# Revit family: TR3105
name_source: partatom
category: Verbindungsmittel
units: mm (PartAtom-declared; Revit-internal decimal feet)

## family parameters
Arbeitsebenenbasiert = Nein
Beim Laden mit Abzugskörper schneiden = Nein
Gemeinsam genutzt = Nein
Immer vertikal = Nein
OmniClass-Nummer = 23.25.10.27.11.21
OmniClass-Titel = Reinforcement Couplers

## types (10) — shared parameters
Endenbearbeitung 1 = Mit Gewinde
Endenbearbeitung 2 = Mit Gewinde
Hersteller = Stahlwerk Annahütte Max Aicher GmbH Co.KG
Modell = TR 3105=TR3014+TR3013
TR3105-G_Vis = Ja
TR3105_Vis = Ja
Typenbild = TR3105.png
Typenkommentare = TR 3105 - Spannschloss
URL = http//:www.annahuette.com

## per-type parameters (varying)
| type | Außendurchmesser | Beschreibung | Einfassung Stab 1 | Einfassung Stab 2 | Gesamtlänge | Körper | Pos_TR3014 | Stabgröße 1 | Stabgröße 2 | TR3013-L0 | TR3013-Lm | TR3013-Lw | TR3013-SW | TR3013-ød | TR3014-L | TR3014-L1 | TR3014-L2 | TR3014-SW | TR3105-G | TR3105-minA | TR3105-ød |
| TR 3105-ø18 | 41 mm  [stored 0.134514 ft] | TR3105-ø18 | 50 mm  [stored 0.164042 ft] | 60 mm  [stored 0.19685 ft] | 175 mm | 1,34 kg | 73 mm | SAS 670 - ø18 | SAS 670 - ø18 | 15 mm  [stored 0.0492126 ft] | 45 mm  [stored 0.147638 ft] | 60 mm  [stored 0.19685 ft] | 41 mm  [stored 0.134514 ft] | 21 mm  [stored 0.0688976 ft] | 145 mm  [stored 0.475722 ft] | 50 mm  [stored 0.164042 ft] | 45 mm  [stored 0.147638 ft] | 41 mm  [stored 0.134514 ft] | 1,34 kg | 30 mm  [stored 0.0984252 ft] | 18 mm  [stored 0.0590551 ft] |
| TR 3105-ø22 | 46 mm  [stored 0.150919 ft] | TR3105-ø22 | 55 mm  [stored 0.180446 ft] | 65 mm  [stored 0.213255 ft] | 190 mm | 1,78 kg | 80 mm  [stored 0.262467 ft] | SAS 670 - ø22 | SAS 670 - ø22 | 15 mm  [stored 0.0492126 ft] | 50 mm  [stored 0.164042 ft] | 65 mm  [stored 0.213255 ft] | 46 mm  [stored 0.150919 ft] | 25 mm  [stored 0.082021 ft] | 160 mm | 55 mm  [stored 0.180446 ft] | 50 mm  [stored 0.164042 ft] | 46 mm  [stored 0.150919 ft] | 1,78 kg | 35 mm  [stored 0.114829 ft] | 22 mm  [stored 0.0721785 ft] |
| TR 3105-ø25 | 55 mm  [stored 0.180446 ft] | TR3105-ø25 | 60 mm  [stored 0.19685 ft] | 70 mm  [stored 0.229659 ft] | 205 mm | 2,94 kg | 88 mm | SAS 670 - ø25 | SAS 670 - ø25 | 15 mm  [stored 0.0492126 ft] | 55 mm  [stored 0.180446 ft] | 70 mm  [stored 0.229659 ft] | 55 mm  [stored 0.180446 ft] | 28 mm  [stored 0.0918635 ft] | 175 mm | 60 mm  [stored 0.19685 ft] | 55 mm  [stored 0.180446 ft] | 55 mm  [stored 0.180446 ft] | 2,94 kg | 40 mm  [stored 0.131234 ft] | 25 mm  [stored 0.082021 ft] |
| TR 3105-ø28 | 50 mm  [stored 0.164042 ft] | TR3105-ø28 | 65 mm  [stored 0.213255 ft] | 80 mm  [stored 0.262467 ft] | 225 mm | 3,74 kg | 95 mm | SAS 670 - ø28 | SAS 670 - ø28 | 20 mm  [stored 0.0656168 ft] | 60 mm  [stored 0.19685 ft] | 80 mm  [stored 0.262467 ft] | 60 mm  [stored 0.19685 ft] | 31 mm  [stored 0.101706 ft] | 190 mm | 65 mm  [stored 0.213255 ft] | 60 mm  [stored 0.19685 ft] | 50 mm  [stored 0.164042 ft] | 3,74 kg | 45 mm  [stored 0.147638 ft] | 28 mm  [stored 0.0918635 ft] |
| TR 3105-ø30 | 65 mm  [stored 0.213255 ft] | TR3105-ø30 | 70 mm  [stored 0.229659 ft] | 95 mm | 260 mm | 5,11 kg | 108 mm | SAS 670 - ø30 | SAS 670 - ø30 | 25 mm  [stored 0.082021 ft] | 70 mm  [stored 0.229659 ft] | 95 mm | 65 mm  [stored 0.213255 ft] | 33 mm | 215 mm | 70 mm  [stored 0.229659 ft] | 65 mm  [stored 0.213255 ft] | 65 mm  [stored 0.213255 ft] | 5,11 kg | 50 mm  [stored 0.164042 ft] | 30 mm  [stored 0.0984252 ft] |
| TR 3105-ø35 | 80 mm  [stored 0.262467 ft] | TR3105-ø35 | 75 mm | 100 mm  [stored 0.328084 ft] | 275 mm | 8,27 kg | 115 mm  [stored 0.377297 ft] | SAS 670 - ø35 | SAS 670 - ø35 | 25 mm  [stored 0.082021 ft] | 75 mm | 100 mm  [stored 0.328084 ft] | 80 mm  [stored 0.262467 ft] | 38 mm  [stored 0.124672 ft] | 230 mm | 75 mm | 75 mm | 80 mm  [stored 0.262467 ft] | 8,27 kg | 55 mm  [stored 0.180446 ft] | 35 mm  [stored 0.114829 ft] |
| TR 3105-ø43 | 90 mm  [stored 0.295276 ft] | TR3105-ø43 | 100 mm  [stored 0.328084 ft] | 115 mm  [stored 0.377297 ft] | 335 mm | 15,14 kg | 140 mm  [stored 0.459318 ft] | SAS 670 - ø43 | SAS 670 - ø43 | 25 mm  [stored 0.082021 ft] | 90 mm  [stored 0.295276 ft] | 115 mm  [stored 0.377297 ft] | 90 mm  [stored 0.295276 ft] | 46 mm  [stored 0.150919 ft] | 280 mm | 100 mm  [stored 0.328084 ft] | 90 mm  [stored 0.295276 ft] | 90 mm  [stored 0.295276 ft] | 15,14 kg | 60 mm  [stored 0.19685 ft] | 43 mm  [stored 0.141076 ft] |
| TR 3105-ø50 | 100 mm  [stored 0.328084 ft] | TR3105-ø50 | 100 mm  [stored 0.328084 ft] | 125 mm  [stored 0.410105 ft] | 350 mm | 19,04 kg | 150 mm | SAS 670 - ø50 | SAS 670 - ø50 | 25 mm  [stored 0.082021 ft] | 100 mm  [stored 0.328084 ft] | 125 mm  [stored 0.410105 ft] | 75 mm | 53 mm | 300 mm | 100 mm  [stored 0.328084 ft] | 100 mm  [stored 0.328084 ft] | 100 mm  [stored 0.328084 ft] | 19,04 kg | 75 mm | 50 mm  [stored 0.164042 ft] |
| TR 3105-ø57,5 | 100 mm  [stored 0.328084 ft] | TR3105-ø57,5 | 125 mm  [stored 0.410105 ft] | 135 mm  [stored 0.442913 ft] | 405 mm | 24,46 kg | 173 mm | SAS 670 - ø57,5 | SAS 670 - ø57,5 | 35 mm  [stored 0.114829 ft] | 100 mm  [stored 0.328084 ft] | 135 mm  [stored 0.442913 ft] | 100 mm  [stored 0.328084 ft] | 61 mm | 345 mm | 125 mm  [stored 0.410105 ft] | 100 mm  [stored 0.328084 ft] | 100 mm  [stored 0.328084 ft] | 24,46 kg | 75 mm | 58 mm |
| TR 3105-ø63,5 | 100 mm  [stored 0.328084 ft] | TR3105-ø63,5 | 140 mm  [stored 0.459318 ft] | 140 mm  [stored 0.459318 ft] | 425 mm | 21,56 kg | 183 mm | SAS 670 - ø63,5 | SAS 670 - ø63,5 | 35 mm  [stored 0.114829 ft] | 105 mm  [stored 0.344488 ft] | 140 mm  [stored 0.459318 ft] | 100 mm  [stored 0.328084 ft] | 46 mm  [stored 0.150919 ft] | 365 mm | 140 mm  [stored 0.459318 ft] | 105 mm  [stored 0.344488 ft] | 100 mm  [stored 0.328084 ft] | 21,56 kg | 80 mm  [stored 0.262467 ft] | 43 mm  [stored 0.141076 ft] |

note: [stored X ft] marks values corroborated as IEEE doubles in the binary element streams (Revit-internal decimal feet)
